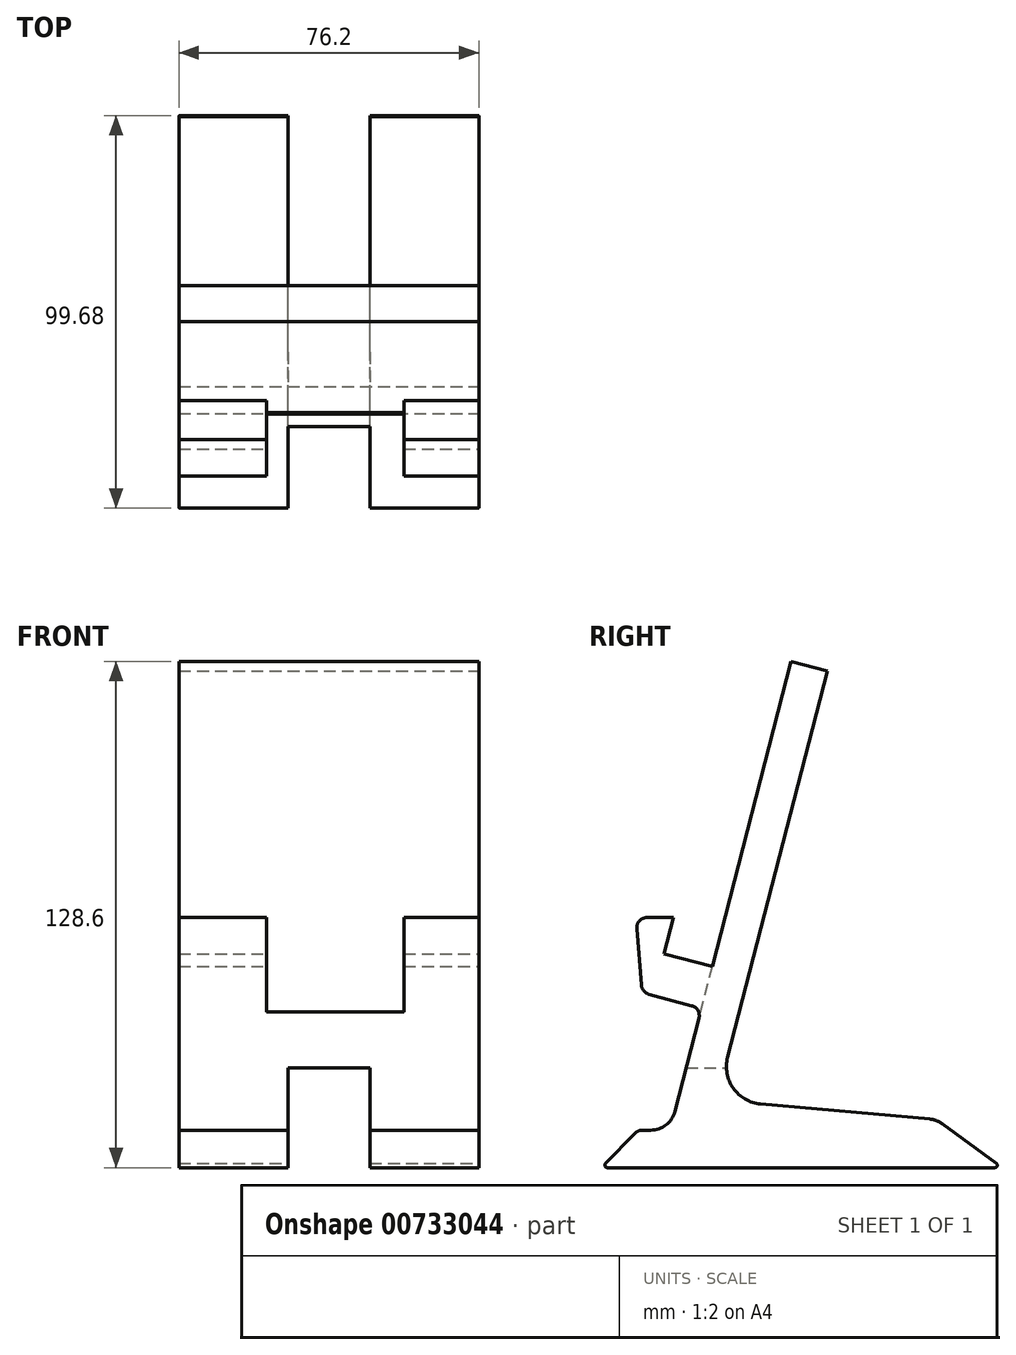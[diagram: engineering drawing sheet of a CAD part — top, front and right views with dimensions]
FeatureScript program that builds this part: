
annotation { "Feature Type Name" : "Feature", "Feature Type Description" : "" }
export const myFeature = defineFeature(function(context is Context, id is Id, definition is map)
    precondition{}
    {
        {
            var Q0;
            Q0=qCreatedBy(makeId("Top.planeOp"),FACE);
            var sketch = newSketch(context, id + "F0", { "sketchPlane" : qUnion([Q0])});
            skLineSegment(sketch, "E0.bottom", {"start": v(-38.1, 50.8) * mm, "end": v(38.1, 50.8) * mm});
            skLineSegment(sketch, "E0.top", {"start": v(-38.1, -50.8) * mm, "end": v(38.1, -50.8) * mm});
            skLineSegment(sketch, "E0.left", {"start": v(-38.1, 50.8) * mm, "end": v(-38.1, -50.8) * mm});
            skLineSegment(sketch, "E0.right", {"start": v(38.1, 50.8) * mm, "end": v(38.1, -50.8) * mm});
            skPoint(sketch, "E0.middle", {"position": v(0, 0) * mm});
            skSolve(sketch);
        }
        {
            var Q0;
            Q0=makeQuery(id+"F0.imprint","IMPRINT",FACE,{"disambiguationData":[TD([[makeQuery(id+"F0.imprint","IMPRINT",EDGE,{"derivedFrom":sQuery(id+"F0.wireOp",EDGE,"E0.bottom")}),-1.0]])]});
            extrude(context, id + "F1", {"entities" : qUnion([Q0]), "depth" : 133.35 * mm, "offsetDistance" : 25.4 * mm});
        }
        {
            var Q0;
            Q0=makeQuery(id+"F1.opExtrude","SWEPT_FACE",FACE,{"disambiguationData":[OSD([sQuery(id+"F0.wireOp",EDGE,"E0.right")])]});
            var sketch = newSketch(context, id + "F2", { "sketchPlane" : qUnion([Q0])});
            skLineSegment(sketch, "E1", {"start": v(50.8, 0) * mm, "end": v(50.8, 133.35) * mm});
            skLineSegment(sketch, "E2", {"start": v(-42.28, 8.76) * mm, "end": v(-49.76, 1.06) * mm});
            skLineSegment(sketch, "E3", {"start": v(-49.32, 0) * mm, "end": v(49.11, 0) * mm});
            skPoint(sketch, "E4.visualSharp", {"position": v(50.8, 0) * mm});
            skArc(sketch, "E4.filletArc", {"start": v(49.11, 0) * mm, "mid": v(49.7, 0.4) * mm, "end": v(49.52, 1.1) * mm});
            skPoint(sketch, "E5.visualSharp", {"position": v(-50.8, 0) * mm});
            skArc(sketch, "E5.filletArc", {"start": v(-49.76, 1.06) * mm, "mid": v(-49.9, 0.38) * mm, "end": v(-49.32, 0) * mm});
            skPoint(sketch, "E6.visualSharp", {"position": v(-41.54, 9.53) * mm});
            skLineSegment(sketch, "E7", {"start": v(-40.46, 9.53) * mm, "end": v(-38.3, 9.53) * mm});
            skPoint(sketch, "E8.visualSharp", {"position": v(-40.5, 44.54) * mm});
            skPoint(sketch, "E9.visualSharp", {"position": v(-40.5, 61.54) * mm});
            skArc(sketch, "E10.filletArc", {"start": v(-40.46, 9.53) * mm, "mid": v(-41.45, 9.32) * mm, "end": v(-42.28, 8.76) * mm});
            skLineSegment(sketch, "E11", {"start": v(-2.6, 128.6) * mm, "end": v(6.59, 126.13) * mm, "construction": true});
            skLineSegment(sketch, "E12", {"start": v(-2.6, 128.6) * mm, "end": v(6.59, 126.13) * mm});
            skLineSegment(sketch, "E13", {"start": v(-26.03, 37.96) * mm, "end": v(-32.15, 14.29) * mm});
            skPoint(sketch, "E14.visualSharp", {"position": v(-33.38, 9.53) * mm});
            skArc(sketch, "E14.filletArc", {"start": v(-38.3, 9.53) * mm, "mid": v(-34.41, 10.85) * mm, "end": v(-32.15, 14.29) * mm});
            skLineSegment(sketch, "E15", {"start": v(-10.38, 16.19) * mm, "end": v(32.58, 12.34) * mm});
            skLineSegment(sketch, "E16", {"start": v(35.75, 11.14) * mm, "end": v(49.52, 1.1) * mm});
            skPoint(sketch, "E17.visualSharp", {"position": v(34.33, 12.18) * mm});
            skArc(sketch, "E17.filletArc", {"start": v(35.75, 11.14) * mm, "mid": v(34.25, 11.96) * mm, "end": v(32.58, 12.34) * mm});
            skLineSegment(sketch, "E18", {"start": v(50.8, 73.73) * mm, "end": v(50.8, 66.27) * mm});
            skLineSegment(sketch, "E19", {"start": v(50.8, 128.6) * mm, "end": v(50.8, 0) * mm});
            skPoint(sketch, "E20", {"position": v(-25.38, 40.48) * mm});
            skLineSegment(sketch, "E21", {"start": v(6.59, 126.13) * mm, "end": v(-18.75, 28.06) * mm});
            skArc(sketch, "E22.filletArc", {"start": v(-18.75, 28.06) * mm, "mid": v(-17.32, 20.19) * mm, "end": v(-10.38, 16.19) * mm});
            skLineSegment(sketch, "E23", {"start": v(-2.6, 128.6) * mm, "end": v(-22.62, 51.15) * mm});
            skLineSegment(sketch, "E24", {"start": v(-22.62, 51.15) * mm, "end": v(-34.92, 54.33) * mm});
            skLineSegment(sketch, "E25", {"start": v(-34.92, 54.33) * mm, "end": v(-32.54, 63.55) * mm});
            skLineSegment(sketch, "E26", {"start": v(-32.54, 63.55) * mm, "end": v(-39.21, 63.55) * mm});
            skLineSegment(sketch, "E27", {"start": v(-41.83, 60.71) * mm, "end": v(-40.65, 46.38) * mm});
            skLineSegment(sketch, "E28", {"start": v(-38.71, 44.06) * mm, "end": v(-27.9, 41.15) * mm});
            skPoint(sketch, "E29.visualSharp", {"position": v(-42.06, 63.55) * mm});
            skArc(sketch, "E29.filletArc", {"start": v(-39.21, 63.55) * mm, "mid": v(-41.14, 62.7) * mm, "end": v(-41.83, 60.71) * mm});
            skArc(sketch, "E30.filletArc", {"start": v(-40.65, 46.38) * mm, "mid": v(-40.05, 44.91) * mm, "end": v(-38.71, 44.06) * mm});
            skArc(sketch, "E31.filletArc", {"start": v(-26.03, 37.96) * mm, "mid": v(-26.3, 39.94) * mm, "end": v(-27.9, 41.15) * mm});
            skLineSegment(sketch, "E32", {"start": v(-50.8, 0) * mm, "end": v(-50.8, 133.35) * mm});
            skSolve(sketch);
        }
        {
            var Q0;
            {var subQ4=sQuery(id+"F2.wireOp",EDGE,"E1");Q0=makeQuery(id+"F2.imprint","IMPRINT",FACE,{"disambiguationData":[TD([[makeQuery(id+"F2.imprint","IMPRINT",EDGE,{"derivedFrom":subQ4}),-1.0]])]});}
            extrude(context, id + "F3", {"entities" : qUnion([Q0]), "operationType" : NewBodyOperationType.REMOVE, "endBound" : BoundingType.THROUGH_ALL, "oppositeDirection" : true, "depth" : 25.4 * mm, "offsetDistance" : 25.4 * mm});
        }
        {
            var Q0;
            Q0=makeQuery(id+"F3.boolean.opBoolean","COPY",FACE,{"derivedFrom":makeQuery(id+"F3.opExtrude","SWEPT_FACE",FACE,{"disambiguationData":[OSD([sQuery(id+"F2.wireOp",EDGE,"E23")])]})});
            var sketch = newSketch(context, id + "F4", { "sketchPlane" : qUnion([Q0])});
            skLineSegment(sketch, "E33", {"start": v(-15.92, 83.07) * mm, "end": v(19.05, 73.93) * mm});
            skLineSegment(sketch, "E34", {"start": v(19.05, 73.93) * mm, "end": v(19.05, 31.73) * mm});
            skLineSegment(sketch, "E35.bottom", {"start": v(-18.15, -55.44) * mm, "end": v(19.95, -55.44) * mm});
            skLineSegment(sketch, "E35.top", {"start": v(-18.15, -97.35) * mm, "end": v(19.95, -97.35) * mm});
            skLineSegment(sketch, "E35.left", {"start": v(-18.15, -55.44) * mm, "end": v(-18.15, -97.35) * mm});
            skLineSegment(sketch, "E35.right", {"start": v(19.95, -97.35) * mm, "end": v(19.95, -55.44) * mm});
            skLineSegment(sketch, "E36.bottom", {"start": v(-21.11, -55.6) * mm, "end": v(16.99, -55.6) * mm});
            skLineSegment(sketch, "E36.top", {"start": v(-21.11, -93.74) * mm, "end": v(16.99, -93.74) * mm});
            skLineSegment(sketch, "E36.left", {"start": v(-21.11, -55.6) * mm, "end": v(-21.11, -93.74) * mm});
            skLineSegment(sketch, "E36.right", {"start": v(16.99, -93.74) * mm, "end": v(16.99, -55.6) * mm});
            skPoint(sketch, "E37.orphan", {"position": v(19.05, 35.02) * mm});
            skLineSegment(sketch, "E38", {"start": v(19.05, 31.73) * mm, "end": v(-15.92, 31.73) * mm});
            skLineSegment(sketch, "E39", {"start": v(-15.92, 31.73) * mm, "end": v(-15.92, 83.07) * mm});
            skSolve(sketch);
        }
        {
            var Q0;
            {var subQ0=sQuery(id+"F4.wireOp",EDGE,"E33");Q0=makeQuery(id+"F4.imprint","IMPRINT",FACE,{"disambiguationData":[TD([[makeQuery(id+"F4.imprint","IMPRINT",EDGE,{"derivedFrom":subQ0}),-1.0]])]});}
            var Q1;
            {var subQ0=sQuery(id+"F4.wireOp",EDGE,"TYNmVz5s-obJO-t62Y-as0B-igR563DwM9H3");var subQ1=sQuery(id+"F4.wireOp",EDGE,"E34");var subQ2=makeQuery(id+"F4.imprint","INTERSECT",VERTEX,{"derivedFrom":[subQ1,subQ0]});Q1=makeQuery(id+"F4.imprint","IMPRINT",FACE,{"disambiguationData":[TD([[makeQuery(id+"F4.imprint","IMPRINT",EDGE,{"disambiguationData":[TD([[subQ2,1.0]])],"derivedFrom":subQ1}),-1.0]])]});}
            extrude(context, id + "F5", {"entities" : qUnion([Q0, Q1]), "operationType" : NewBodyOperationType.REMOVE, "depth" : 25.4 * mm, "offsetDistance" : 25.4 * mm});
        }
        {
            var Q0;
            Q0=makeQuery(id+"F1.opExtrude","CAP_FACE",FACE,{"disambiguationData":[OSD([sQuery(id+"F0.wireOp",EDGE,"E0.bottom"),sQuery(id+"F0.wireOp",EDGE,"E0.top"),sQuery(id+"F0.wireOp",EDGE,"E0.left"),sQuery(id+"F0.wireOp",EDGE,"E0.right")])],"isStart":true});
            var sketch = newSketch(context, id + "F6", { "sketchPlane" : qUnion([Q0])});
            skLineSegment(sketch, "E40.bottom", {"start": v(-10.42, 56.63) * mm, "end": v(10.42, 56.63) * mm});
            skLineSegment(sketch, "E40.top", {"start": v(-10.42, -56.63) * mm, "end": v(10.42, -56.63) * mm});
            skLineSegment(sketch, "E40.left", {"start": v(-10.42, 56.63) * mm, "end": v(-10.42, -56.63) * mm});
            skLineSegment(sketch, "E40.right", {"start": v(10.42, 56.63) * mm, "end": v(10.42, -56.63) * mm});
            skPoint(sketch, "E40.middle", {"position": v(0, 0) * mm});
            skLineSegment(sketch, "E41", {"start": v(0, 56.63) * mm, "end": v(0, -56.63) * mm, "construction": true});
            skSolve(sketch);
        }
        {
            var Q0;
            Q0 = qSketchRegion(id + "F6", true);
            extrude(context, id + "F7", {"entities" : qUnion([Q0]), "operationType" : NewBodyOperationType.REMOVE, "oppositeDirection" : true, "depth" : 25.4 * mm, "offsetDistance" : 25.4 * mm});
        }
    });
